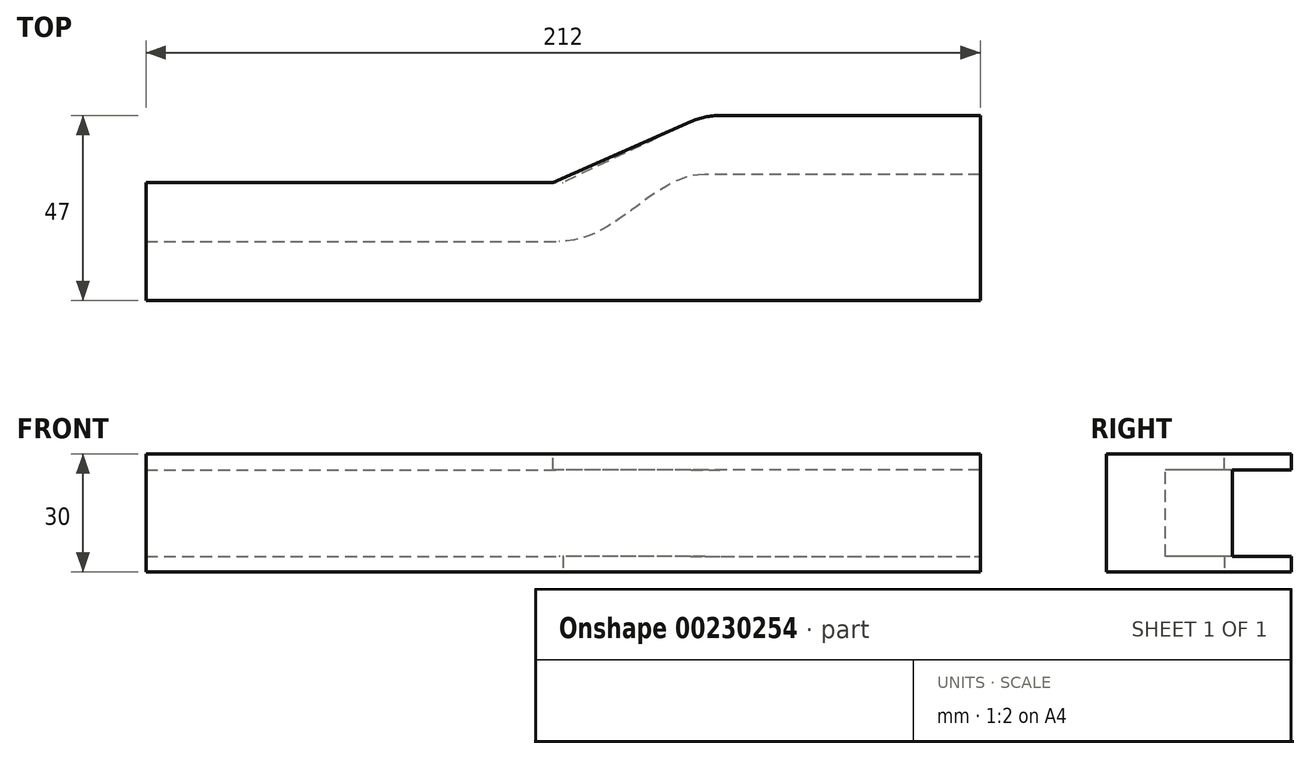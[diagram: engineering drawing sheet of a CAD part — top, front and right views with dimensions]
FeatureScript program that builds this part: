
annotation { "Feature Type Name" : "Feature", "Feature Type Description" : "" }
export const myFeature = defineFeature(function(context is Context, id is Id, definition is map)
    precondition{}
    {
        {
            var Q0;
            Q0=qCreatedBy(makeId("Top.planeOp"),FACE);
            var sketch = newSketch(context, id + "F0", { "sketchPlane" : qUnion([Q0])});
            skLineSegment(sketch, "E0", {"start": v(-81.7, 0) * mm, "end": v(23.3, 0) * mm});
            skLineSegment(sketch, "E1", {"start": v(23.3, 0) * mm, "end": v(23.3, 17) * mm, "construction": true});
            skLineSegment(sketch, "E2", {"start": v(23.3, 17) * mm, "end": v(60.3, 17) * mm, "construction": true});
            skLineSegment(sketch, "E3", {"start": v(60.3, 17) * mm, "end": v(130.3, 17) * mm});
            skLineSegment(sketch, "E4", {"start": v(130.3, 17) * mm, "end": v(130.3, -15) * mm});
            skLineSegment(sketch, "E5", {"start": v(130.3, -15) * mm, "end": v(-81.7, -15) * mm});
            skLineSegment(sketch, "E6", {"start": v(-81.7, -15) * mm, "end": v(-81.7, 0) * mm});
            skFitSpline(sketch, "E7", {"points": [v(60.3, 17) * mm, v(23.3, 0) * mm], "startDerivative": vector(-39.76, 0) * mm, "endDerivative": vector(-44.92, 0) * mm});
            skSolve(sketch);
        }
        {
            var Q0;
            Q0=makeQuery(id+"F0.imprint","IMPRINT",FACE,{"disambiguationData":[TD([[makeQuery(id+"F0.imprint","IMPRINT",EDGE,{"derivedFrom":sQuery(id+"F0.wireOp",EDGE,"E0")}),-1.0]])]});
            var Q1;
            Q1=qSketchRegion(id+"F0",true);
            extrude(context, id + "F1", {"entities" : qUnion([Q0, Q1]), "oppositeDirection" : true, "depth" : 28 * mm});
        }
        {
            var Q0;
            Q0=makeQuery(id+"F1.opExtrude","SWEPT_FACE",FACE,{"disambiguationData":[OSD([sQuery(id+"F0.wireOp",EDGE,"E0")])]});
            var sketch = newSketch(context, id + "F2", { "sketchPlane" : qUnion([Q0])});
            skLineSegment(sketch, "E8.bottom", {"start": v(81.7, 0) * mm, "end": v(-130.2, 0) * mm});
            skLineSegment(sketch, "E8.top", {"start": v(81.7, -3) * mm, "end": v(-130.2, -3) * mm});
            skLineSegment(sketch, "E8.left", {"start": v(81.7, 0) * mm, "end": v(81.7, -3) * mm});
            skLineSegment(sketch, "E8.right", {"start": v(-130.2, 0) * mm, "end": v(-130.2, -3) * mm});
            skLineSegment(sketch, "E9.bottom", {"start": v(81.7, -28) * mm, "end": v(-130.2, -28) * mm});
            skLineSegment(sketch, "E9.top", {"start": v(81.7, -25) * mm, "end": v(-130.2, -25) * mm});
            skLineSegment(sketch, "E9.left", {"start": v(81.7, -28) * mm, "end": v(81.7, -25) * mm});
            skLineSegment(sketch, "E9.right", {"start": v(-130.2, -28) * mm, "end": v(-130.2, -25) * mm});
            skSolve(sketch);
        }
        {
            var Q0;
            Q0=qSketchRegion(id+"F2",true);
            extrude(context, id + "F3", {"entities" : qUnion([Q0]), "operationType" : NewBodyOperationType.ADD, "depth" : 15 * mm});
        }
        {
            var Q0;
            Q0=makeQuery(id+"F1.opExtrude","SWEPT_FACE",FACE,{"disambiguationData":[OSD([sQuery(id+"F0.wireOp",EDGE,"E3")])]});
            var sketch = newSketch(context, id + "F4", { "sketchPlane" : qUnion([Q0])});
            skLineSegment(sketch, "E10.bottom", {"start": v(-60.3, -28) * mm, "end": v(-130.3, -28) * mm});
            skLineSegment(sketch, "E10.top", {"start": v(-60.3, -25) * mm, "end": v(-130.3, -25) * mm});
            skLineSegment(sketch, "E10.left", {"start": v(-60.3, -28) * mm, "end": v(-60.3, -25) * mm});
            skLineSegment(sketch, "E10.right", {"start": v(-130.3, -28) * mm, "end": v(-130.3, -25) * mm});
            skLineSegment(sketch, "E11.bottom", {"start": v(-130.3, 0) * mm, "end": v(-60.3, 0) * mm});
            skLineSegment(sketch, "E11.top", {"start": v(-130.3, -3) * mm, "end": v(-60.3, -3) * mm});
            skLineSegment(sketch, "E11.left", {"start": v(-130.3, 0) * mm, "end": v(-130.3, -3) * mm});
            skLineSegment(sketch, "E11.right", {"start": v(-60.3, 0) * mm, "end": v(-60.3, -3) * mm});
            skSolve(sketch);
        }
        {
            var Q0;
            Q0=qSketchRegion(id+"F4",true);
            extrude(context, id + "F5", {"entities" : qUnion([Q0]), "operationType" : NewBodyOperationType.ADD, "depth" : 15 * mm});
        }
        {
            var Q0;
            Q0=makeQuery(id+"F5.boolean.opBoolean","MERGE",FACE,{"derivedFrom":[makeQuery(id+"F3.boolean.opBoolean","MERGE",FACE,{"derivedFrom":[makeQuery(id+"F1.opExtrude","CAP_FACE",FACE,{"disambiguationData":[OSD([sQuery(id+"F0.wireOp",EDGE,"E0"),sQuery(id+"F0.wireOp",EDGE,"E3"),sQuery(id+"F0.wireOp",EDGE,"E4"),sQuery(id+"F0.wireOp",EDGE,"E5"),sQuery(id+"F0.wireOp",EDGE,"E6"),sQuery(id+"F0.wireOp",EDGE,"E7")])],"isStart":true}),makeQuery(id+"F3.opExtrude","SWEPT_FACE",FACE,{"disambiguationData":[OSD([sQuery(id+"F2.wireOp",EDGE,"E8.bottom")])]})]}),makeQuery(id+"F5.opExtrude","SWEPT_FACE",FACE,{"disambiguationData":[OSD([sQuery(id+"F4.wireOp",EDGE,"E11.bottom")])]})]});
            var sketch = newSketch(context, id + "F6", { "sketchPlane" : qUnion([Q0])});
            skLineSegment(sketch, "E12", {"start": v(60.3, 32) * mm, "end": v(21.74, 15) * mm});
            skLineSegment(sketch, "E13", {"start": v(21.74, 15) * mm, "end": v(26.04, -15) * mm});
            skLineSegment(sketch, "E14", {"start": v(26.04, -15) * mm, "end": v(64.8, 0) * mm});
            skLineSegment(sketch, "E15", {"start": v(64.8, 0) * mm, "end": v(60.3, 32) * mm});
            skSolve(sketch);
        }
        {
            var Q0;
            Q0=qSketchRegion(id+"F6",true);
            extrude(context, id + "F7", {"entities" : qUnion([Q0]), "operationType" : NewBodyOperationType.ADD, "oppositeDirection" : true, "depth" : 3 * mm});
        }
        {
            var Q0;
            {var subQ0=sQuery(id+"F4.wireOp",EDGE,"E11.right");Q0=makeQuery(id+"F7.boolean.opBoolean","MERGE",EDGE,{"derivedFrom":[makeQuery(id+"F5.opExtrude","CAP_EDGE",EDGE,{"disambiguationData":[OSD([subQ0])],"isStart":false}),makeQuery(id+"F7.opExtrude","SWEPT_EDGE",EDGE,{"disambiguationData":[OSD([sQuery(id+"F4.wireOp",EDGE,"E11.bottom"),subQ0,sQuery(id+"F6.wireOp",EDGE,"E12"),sQuery(id+"F6.wireOp",EDGE,"E15")])]})]});}
            var Q1;
            Q1=makeQuery(id+"F7.opExtrude","SWEPT_EDGE",EDGE,{"disambiguationData":[OSD([sQuery(id+"F2.wireOp",EDGE,"E8.bottom"),sQuery(id+"F6.wireOp",EDGE,"E12"),sQuery(id+"F6.wireOp",EDGE,"E13")])]});
            fillet(context, id + "F8", {"entities" : qUnion([Q0, Q1]), "radius" : 18.22 * mm, "tangentPropagation" : true, "allowEdgeOverflow" : false});
        }
        {
            var Q0;
            Q0=makeQuery(id+"F5.boolean.opBoolean","MERGE",FACE,{"derivedFrom":[makeQuery(id+"F3.boolean.opBoolean","MERGE",FACE,{"derivedFrom":[makeQuery(id+"F1.opExtrude","CAP_FACE",FACE,{"disambiguationData":[OSD([sQuery(id+"F0.wireOp",EDGE,"E0"),sQuery(id+"F0.wireOp",EDGE,"E3"),sQuery(id+"F0.wireOp",EDGE,"E4"),sQuery(id+"F0.wireOp",EDGE,"E5"),sQuery(id+"F0.wireOp",EDGE,"E6"),sQuery(id+"F0.wireOp",EDGE,"E7")])],"isStart":false}),makeQuery(id+"F3.opExtrude","SWEPT_FACE",FACE,{"disambiguationData":[OSD([sQuery(id+"F2.wireOp",EDGE,"E9.bottom")])]})]}),makeQuery(id+"F5.opExtrude","SWEPT_FACE",FACE,{"disambiguationData":[OSD([sQuery(id+"F4.wireOp",EDGE,"E10.bottom")])]})]});
            var sketch = newSketch(context, id + "F9", { "sketchPlane" : qUnion([Q0])});
            skLineSegment(sketch, "E16", {"start": v(60.3, -32) * mm, "end": v(24.3, -15) * mm});
            skPoint(sketch, "E16.endSnap0", {"position": v(24.3, 15) * mm});
            skPoint(sketch, "E17.orphan", {"position": v(60.3, 15) * mm});
            skLineSegment(sketch, "E18", {"start": v(60.3, -32) * mm, "end": v(60.3, -17) * mm});
            skLineSegment(sketch, "E19", {"start": v(60.3, -17) * mm, "end": v(52.3, -15) * mm});
            skLineSegment(sketch, "E20", {"start": v(52.3, -15) * mm, "end": v(24.3, -15) * mm});
            skSolve(sketch);
        }
        {
            var Q0;
            Q0=qSketchRegion(id+"F9",true);
            extrude(context, id + "F10", {"entities" : qUnion([Q0]), "operationType" : NewBodyOperationType.ADD, "oppositeDirection" : true, "depth" : 3 * mm});
        }
        {
            var Q0;
            Q0=makeQuery(id+"F10.boolean.opBoolean","MERGE",EDGE,{"derivedFrom":[makeQuery(id+"F5.opExtrude","CAP_EDGE",EDGE,{"disambiguationData":[OSD([sQuery(id+"F4.wireOp",EDGE,"E10.left")])],"isStart":false}),makeQuery(id+"F10.opExtrude","SWEPT_EDGE",EDGE,{"disambiguationData":[OSD([sQuery(id+"F4.wireOp",EDGE,"E10.bottom"),sQuery(id+"F9.wireOp",EDGE,"E16"),sQuery(id+"F9.wireOp",EDGE,"E18")])]})]});
            var Q1;
            Q1=makeQuery(id+"F10.opExtrude","SWEPT_EDGE",EDGE,{"disambiguationData":[OSD([sQuery(id+"F2.wireOp",EDGE,"E9.bottom"),sQuery(id+"F9.wireOp",EDGE,"E16"),sQuery(id+"F9.wireOp",EDGE,"E20")])]});
            fillet(context, id + "F11", {"entities" : qUnion([Q0, Q1]), "radius" : 18.22 * mm, "tangentPropagation" : true, "allowEdgeOverflow" : false});
        }
        {
            var Q0;
            Q0=makeQuery(id+"F7.boolean.opBoolean","MERGE",FACE,{"derivedFrom":[makeQuery(id+"F5.boolean.opBoolean","MERGE",FACE,{"derivedFrom":[makeQuery(id+"F3.boolean.opBoolean","MERGE",FACE,{"derivedFrom":[makeQuery(id+"F1.opExtrude","CAP_FACE",FACE,{"disambiguationData":[OSD([sQuery(id+"F0.wireOp",EDGE,"E0"),sQuery(id+"F0.wireOp",EDGE,"E3"),sQuery(id+"F0.wireOp",EDGE,"E4"),sQuery(id+"F0.wireOp",EDGE,"E5"),sQuery(id+"F0.wireOp",EDGE,"E6"),sQuery(id+"F0.wireOp",EDGE,"E7")])],"isStart":true}),makeQuery(id+"F3.opExtrude","SWEPT_FACE",FACE,{"disambiguationData":[OSD([sQuery(id+"F2.wireOp",EDGE,"E8.bottom")])]})]}),makeQuery(id+"F5.opExtrude","SWEPT_FACE",FACE,{"disambiguationData":[OSD([sQuery(id+"F4.wireOp",EDGE,"E11.bottom")])]})]}),makeQuery(id+"F7.opExtrude","CAP_FACE",FACE,{"disambiguationData":[OSD([sQuery(id+"F6.wireOp",EDGE,"E12"),sQuery(id+"F6.wireOp",EDGE,"E13"),sQuery(id+"F6.wireOp",EDGE,"E14"),sQuery(id+"F6.wireOp",EDGE,"E15")])],"isStart":true})]});
            var sketch = newSketch(context, id + "F12", { "sketchPlane" : qUnion([Q0])});
            skLineSegment(sketch, "E21.0.0", {"start": v(130.3, 32) * mm, "end": v(64.13, 32) * mm});
            skArc(sketch, "E21.0.1", {"start": v(64.13, 32) * mm, "mid": v(60.38, 31.6) * mm, "end": v(56.78, 30.45) * mm});
            skLineSegment(sketch, "E21.0.2", {"start": v(56.78, 30.45) * mm, "end": v(25.25, 16.55) * mm});
            skArc(sketch, "E21.0.3", {"start": v(25.25, 16.55) * mm, "mid": v(21.66, 15.4) * mm, "end": v(17.9, 15) * mm});
            skLineSegment(sketch, "E21.0.4", {"start": v(17.9, 15) * mm, "end": v(-81.7, 15) * mm});
            skLineSegment(sketch, "E21.0.5", {"start": v(-81.7, 15) * mm, "end": v(-81.7, -15) * mm});
            skLineSegment(sketch, "E21.0.6", {"start": v(-81.7, -15) * mm, "end": v(130.3, -15) * mm});
            skLineSegment(sketch, "E21.0.7", {"start": v(130.3, -15) * mm, "end": v(130.3, 32) * mm});
            skSolve(sketch);
        }
        {
            var Q0;
            Q0=makeQuery(id+"F12.imprint","IMPRINT",FACE,{"disambiguationData":[TD([[makeQuery(id+"F12.imprint","IMPRINT",EDGE,{"derivedFrom":sQuery(id+"F12.wireOp",EDGE,"E21.0.0")}),-1.0]])]});
            extrude(context, id + "F13", {"entities" : qUnion([Q0]), "operationType" : NewBodyOperationType.ADD, "depth" : 1 * mm});
        }
        {
            var Q0;
            Q0=makeQuery(id+"F10.boolean.opBoolean","MERGE",FACE,{"derivedFrom":[makeQuery(id+"F5.boolean.opBoolean","MERGE",FACE,{"derivedFrom":[makeQuery(id+"F3.boolean.opBoolean","MERGE",FACE,{"derivedFrom":[makeQuery(id+"F1.opExtrude","CAP_FACE",FACE,{"disambiguationData":[OSD([sQuery(id+"F0.wireOp",EDGE,"E0"),sQuery(id+"F0.wireOp",EDGE,"E3"),sQuery(id+"F0.wireOp",EDGE,"E4"),sQuery(id+"F0.wireOp",EDGE,"E5"),sQuery(id+"F0.wireOp",EDGE,"E6"),sQuery(id+"F0.wireOp",EDGE,"E7")])],"isStart":false}),makeQuery(id+"F3.opExtrude","SWEPT_FACE",FACE,{"disambiguationData":[OSD([sQuery(id+"F2.wireOp",EDGE,"E9.bottom")])]})]}),makeQuery(id+"F5.opExtrude","SWEPT_FACE",FACE,{"disambiguationData":[OSD([sQuery(id+"F4.wireOp",EDGE,"E10.bottom")])]})]}),makeQuery(id+"F10.opExtrude","CAP_FACE",FACE,{"disambiguationData":[OSD([sQuery(id+"F9.wireOp",EDGE,"E16"),sQuery(id+"F9.wireOp",EDGE,"E18"),sQuery(id+"F9.wireOp",EDGE,"E19"),sQuery(id+"F9.wireOp",EDGE,"E20")])],"isStart":true})]});
            var sketch = newSketch(context, id + "F14", { "sketchPlane" : qUnion([Q0])});
            skLineSegment(sketch, "E22.0.0", {"start": v(27.99, -16.74) * mm, "end": v(56.6, -30.26) * mm});
            skArc(sketch, "E22.0.1", {"start": v(56.6, -30.26) * mm, "mid": v(60.4, -31.56) * mm, "end": v(64.38, -32) * mm});
            skLineSegment(sketch, "E22.0.2", {"start": v(64.38, -32) * mm, "end": v(130.3, -32) * mm});
            skLineSegment(sketch, "E22.0.3", {"start": v(130.3, -32) * mm, "end": v(130.3, 15) * mm});
            skLineSegment(sketch, "E22.0.4", {"start": v(130.3, 15) * mm, "end": v(-81.7, 15) * mm});
            skLineSegment(sketch, "E22.0.5", {"start": v(-81.7, 15) * mm, "end": v(-81.7, -15) * mm});
            skLineSegment(sketch, "E22.0.6", {"start": v(-81.7, -15) * mm, "end": v(20.2, -15) * mm});
            skArc(sketch, "E22.0.7", {"start": v(20.2, -15) * mm, "mid": v(24.2, -15.44) * mm, "end": v(27.99, -16.74) * mm});
            skSolve(sketch);
        }
        {
            var Q0;
            Q0=makeQuery(id+"F14.imprint","IMPRINT",FACE,{"disambiguationData":[TD([[makeQuery(id+"F14.imprint","IMPRINT",EDGE,{"derivedFrom":sQuery(id+"F14.wireOp",EDGE,"E22.0.0")}),-1.0]])]});
            extrude(context, id + "F15", {"entities" : qUnion([Q0]), "operationType" : NewBodyOperationType.ADD, "depth" : 1 * mm});
        }
    });
